# Revit family: FA_ШинаУравниванияПотенциалов_44461_EZETEK
name_source: partatom
category: Системы пожарной сигнализации
revit_build: Autodesk Revit 2017 (Build: 20170118_1100(x64)
units: mm (PartAtom-declared; Revit-internal decimal feet)

## family parameters
Всегда вертикально = Да
На основе рабочей плоскости = Нет
Общий = Нет
При загрузке вырезать с полостями = Нет
Размер круглого соединителя = Использовать радиус
Сохранять ориентацию аннотаций = Нет
Тип детали = Нормальный
Точка расчета площади = Нет

## types (1)
- ШинаУравниванияПотенциалов_44461
    ADSK_Версия Revit = 2017
    ADSK_Единица измерения = шт.
    ADSK_Завод-изготовитель = Ezetek
    ADSK_Код изделия = 44461
    ADSK_Количество = 1
    ADSK_Марка = 44461
    ADSK_Масса = 0.17
    ADSK_Масса_Текст = 0.17
    ADSK_Материал = BIMLIB_Пластик_EZETEK
    ADSK_Наименование = Шина уравнивания потенциалов 10х8х130 мм
    ADSK_Обозначение = 44461
    ADSK_Размер_Длина = 147 мм
    L = 175 мм
    URL = https://ezetek.ru
    W = 52 мм
    Группа модели = Коробки и шины уравнивания потенциалов
    Изготовитель = Ezetek
    Описание = Шина уравнивания потенциалов предназначена для организации дополнительной системы уравнивания потенциалов в квартирах, домах, офисах и производственных помещениях — шина объединяет защитные проводники электрического оборудования и подключается к ГЗШ. Шина уравнивания потенциалов выполнена из латуни и имеет пластиковый кожух.
